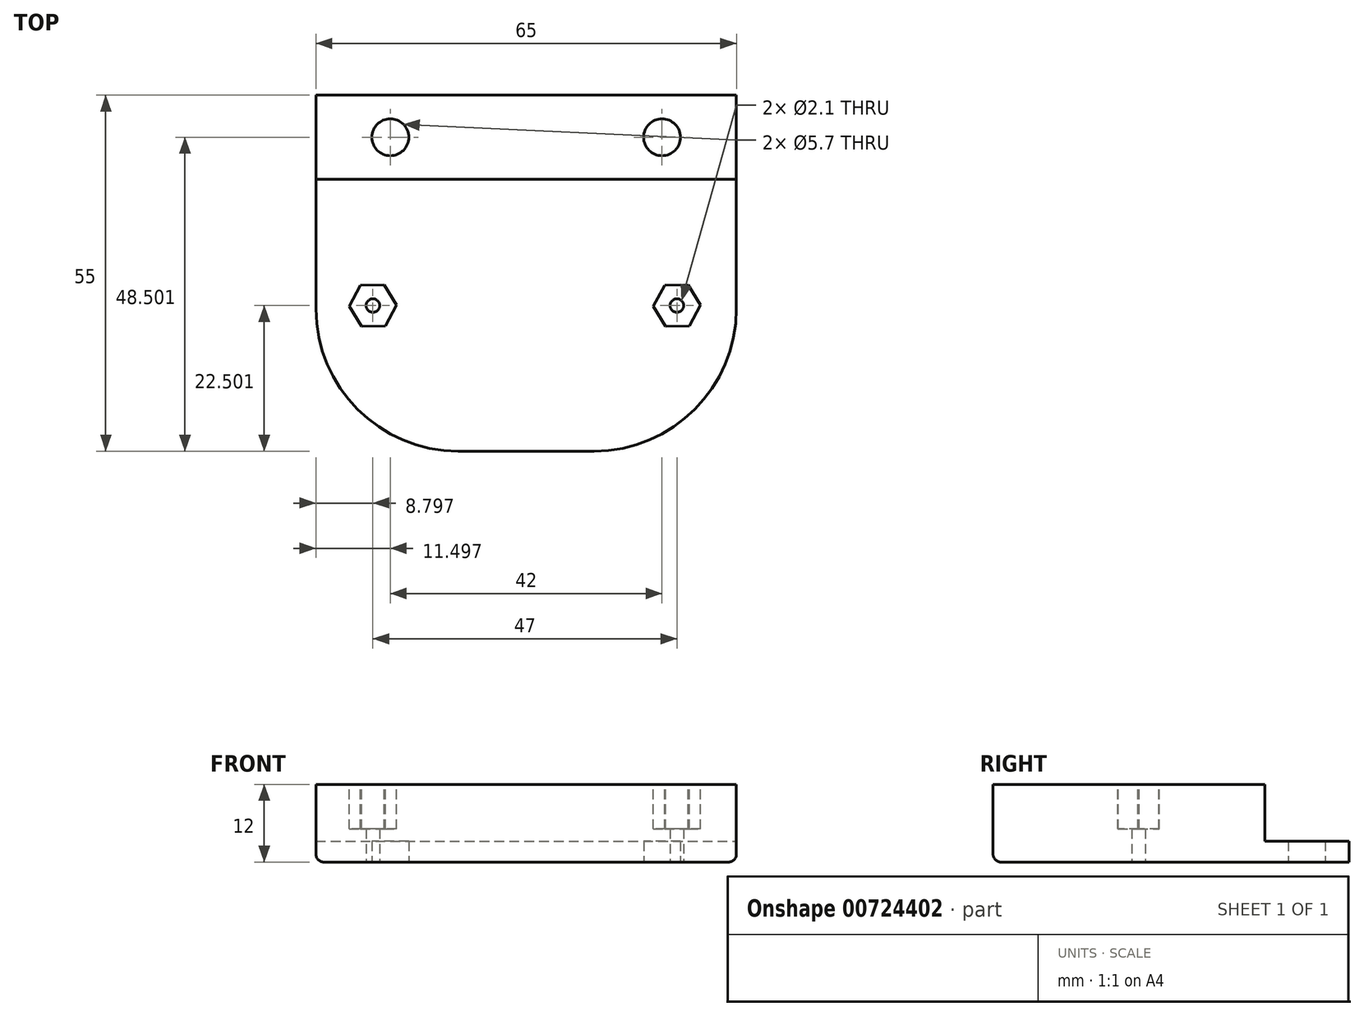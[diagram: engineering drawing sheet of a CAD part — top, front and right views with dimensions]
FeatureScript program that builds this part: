
annotation { "Feature Type Name" : "Feature", "Feature Type Description" : "" }
export const myFeature = defineFeature(function(context is Context, id is Id, definition is map)
    precondition{}
    {
        {
            var Q0;
            Q0=qCreatedBy(makeId("Top.planeOp"),FACE);
            var sketch = newSketch(context, id + "F0", { "sketchPlane" : qUnion([Q0])});
            skLineSegment(sketch, "E0.bottom", {"start": v(-32.1, -2.87) * mm, "end": v(32.9, -2.87) * mm});
            skLineSegment(sketch, "E0.top", {"start": v(-32.1, -17.87) * mm, "end": v(32.9, -17.87) * mm});
            skLineSegment(sketch, "E0.left", {"start": v(-32.1, -2.87) * mm, "end": v(-32.1, -17.87) * mm});
            skLineSegment(sketch, "E0.right", {"start": v(32.9, -2.87) * mm, "end": v(32.9, -17.87) * mm});
            skCircle(sketch, "E1", {"center": v(21.4, -9.37) * mm, "radius": 2.85 * mm});
            skCircle(sketch, "E2", {"center": v(-20.6, -9.37) * mm, "radius": 2.85 * mm});
            skLineSegment(sketch, "E3.top", {"start": v(-10.1, -57.87) * mm, "end": v(10.9, -57.87) * mm});
            skLineSegment(sketch, "E3.left", {"start": v(-32.1, -17.87) * mm, "end": v(-32.1, -35.87) * mm});
            skLineSegment(sketch, "E3.right", {"start": v(32.9, -17.87) * mm, "end": v(32.9, -35.87) * mm});
            skPoint(sketch, "E4.visualSharp", {"position": v(32.9, -57.87) * mm});
            skArc(sketch, "E4.filletArc", {"start": v(10.9, -57.87) * mm, "mid": v(26.45, -51.43) * mm, "end": v(32.9, -35.87) * mm});
            skPoint(sketch, "E5.visualSharp", {"position": v(-32.1, -57.87) * mm});
            skArc(sketch, "E5.filletArc", {"start": v(-32.1, -35.87) * mm, "mid": v(-25.66, -51.43) * mm, "end": v(-10.1, -57.87) * mm});
            skSolve(sketch);
        }
        {
            var Q0;
            Q0 = qSketchRegion(id + "F0", true);
            extrude(context, id + "F1", {"entities" : qUnion([Q0]), "depth" : 12 * mm, "offsetDistance" : 25 * mm});
        }
        {
            var Q0;
            Q0=makeQuery(id+"F1.opExtrude","CAP_FACE",FACE,{"disambiguationData":[OSD([sQuery(id+"F0.wireOp",EDGE,"E0.bottom"),sQuery(id+"F0.wireOp",EDGE,"E0.left"),sQuery(id+"F0.wireOp",EDGE,"E0.right"),sQuery(id+"F0.wireOp",EDGE,"Pb8QJhGn-lq3P-DoKP-Ju5z-BRii3pjlZWMS")])],"isStart":false});
            var sketch = newSketch(context, id + "F2", { "sketchPlane" : qUnion([Q0])});
            skLineSegment(sketch, "E6.bottom", {"start": v(32.9, -15.87) * mm, "end": v(-32.1, -15.87) * mm});
            skLineSegment(sketch, "E6.top", {"start": v(32.9, -2.87) * mm, "end": v(-32.1, -2.87) * mm});
            skLineSegment(sketch, "E6.left", {"start": v(32.9, -15.87) * mm, "end": v(32.9, -2.87) * mm});
            skLineSegment(sketch, "E6.right", {"start": v(-32.1, -15.87) * mm, "end": v(-32.1, -2.87) * mm});
            skSolve(sketch);
        }
        {
            var Q0;
            Q0 = qSketchRegion(id + "F2", true);
            extrude(context, id + "F3", {"entities" : qUnion([Q0]), "operationType" : NewBodyOperationType.REMOVE, "oppositeDirection" : true, "depth" : 8.8 * mm, "offsetDistance" : 25 * mm});
        }
        {
            var Q0;
            Q0=makeQuery(id+"F1.opExtrude","CAP_EDGE",EDGE,{"disambiguationData":[OSD([sQuery(id+"F0.wireOp",EDGE,"E0.left"),sQuery(id+"F0.wireOp",EDGE,"E3.left")])],"isStart":true});
            var Q1;
            Q1=makeQuery(id+"F1.opExtrude","CAP_EDGE",EDGE,{"disambiguationData":[OSD([sQuery(id+"F0.wireOp",EDGE,"E3.top")])],"isStart":true});
            var Q2;
            Q2=makeQuery(id+"F1.opExtrude","CAP_EDGE",EDGE,{"disambiguationData":[OSD([sQuery(id+"F0.wireOp",EDGE,"E0.right"),sQuery(id+"F0.wireOp",EDGE,"E3.right")])],"isStart":true});
            fillet(context, id + "F4", {"entities" : qUnion([Q0, Q1, Q2]), "radius" : 1.2 * mm, "tangentPropagation" : true, "allowEdgeOverflow" : false});
        }
        {
            var Q0;
            Q0=makeQuery(id+"F1.opExtrude","CAP_FACE",FACE,{"disambiguationData":[OSD([sQuery(id+"F0.wireOp",EDGE,"E0.bottom"),sQuery(id+"F0.wireOp",EDGE,"E0.left"),sQuery(id+"F0.wireOp",EDGE,"E0.right"),sQuery(id+"F0.wireOp",EDGE,"E1"),sQuery(id+"F0.wireOp",EDGE,"E2"),sQuery(id+"F0.wireOp",EDGE,"E3.top"),sQuery(id+"F0.wireOp",EDGE,"E3.left"),sQuery(id+"F0.wireOp",EDGE,"E3.right"),sQuery(id+"F0.wireOp",EDGE,"E4.filletArc"),sQuery(id+"F0.wireOp",EDGE,"E5.filletArc")])],"isStart":true});
            var sketch = newSketch(context, id + "F5", { "sketchPlane" : qUnion([Q0])});
            skCircle(sketch, "E7", {"center": v(23.7, 35.37) * mm, "radius": 1.05 * mm});
            skCircle(sketch, "E8", {"center": v(-23.3, 35.37) * mm, "radius": 1.05 * mm});
            skSolve(sketch);
        }
        {
            var Q0;
            Q0 = qSketchRegion(id + "F5", true);
            extrude(context, id + "F6", {"entities" : qUnion([Q0]), "operationType" : NewBodyOperationType.REMOVE, "oppositeDirection" : true, "depth" : 15 * mm, "offsetDistance" : 25 * mm});
        }
        {
            var Q0;
            Q0=makeQuery(id+"F1.opExtrude","CAP_FACE",FACE,{"disambiguationData":[OSD([sQuery(id+"F0.wireOp",EDGE,"E0.bottom"),sQuery(id+"F0.wireOp",EDGE,"E0.left"),sQuery(id+"F0.wireOp",EDGE,"E0.right"),sQuery(id+"F0.wireOp",EDGE,"E1"),sQuery(id+"F0.wireOp",EDGE,"E2"),sQuery(id+"F0.wireOp",EDGE,"E3.top"),sQuery(id+"F0.wireOp",EDGE,"E3.left"),sQuery(id+"F0.wireOp",EDGE,"E3.right"),sQuery(id+"F0.wireOp",EDGE,"E4.filletArc"),sQuery(id+"F0.wireOp",EDGE,"E5.filletArc")])],"isStart":false});
            var sketch = newSketch(context, id + "F7", { "sketchPlane" : qUnion([Q0])});
            skCircle(sketch, "E9.cCircle", {"center": v(23.7, -35.37) * mm, "radius": 3.18 * mm, "construction": true});
            skLineSegment(sketch, "E9.0", {"start": v(27.36, -35.28) * mm, "end": v(25.6, -38.5) * mm});
            skLineSegment(sketch, "E9.1", {"start": v(25.6, -38.5) * mm, "end": v(21.94, -38.59) * mm});
            skLineSegment(sketch, "E9.2", {"start": v(21.94, -38.59) * mm, "end": v(20.03, -35.46) * mm});
            skLineSegment(sketch, "E9.3", {"start": v(20.03, -35.46) * mm, "end": v(21.79, -32.24) * mm});
            skLineSegment(sketch, "E9.4", {"start": v(21.79, -32.24) * mm, "end": v(25.45, -32.15) * mm});
            skLineSegment(sketch, "E9.5", {"start": v(25.45, -32.15) * mm, "end": v(27.36, -35.28) * mm});
            skPoint(sketch, "E9.0.midPoint", {"position": v(26.48, -36.9) * mm});
            skCircle(sketch, "E10.cCircle", {"center": v(-23.3, -35.37) * mm, "radius": 3.18 * mm, "construction": true});
            skLineSegment(sketch, "E10.0", {"start": v(-19.64, -35.28) * mm, "end": v(-21.4, -38.5) * mm});
            skLineSegment(sketch, "E10.1", {"start": v(-21.4, -38.5) * mm, "end": v(-25.06, -38.59) * mm});
            skLineSegment(sketch, "E10.2", {"start": v(-25.06, -38.59) * mm, "end": v(-26.97, -35.46) * mm});
            skLineSegment(sketch, "E10.3", {"start": v(-26.97, -35.46) * mm, "end": v(-25.21, -32.24) * mm});
            skLineSegment(sketch, "E10.4", {"start": v(-25.21, -32.24) * mm, "end": v(-21.55, -32.15) * mm});
            skLineSegment(sketch, "E10.5", {"start": v(-21.55, -32.15) * mm, "end": v(-19.64, -35.28) * mm});
            skPoint(sketch, "E10.0.midPoint", {"position": v(-20.52, -36.9) * mm});
            skSolve(sketch);
        }
        {
            var Q0;
            Q0 = qSketchRegion(id + "F7", true);
            extrude(context, id + "F8", {"entities" : qUnion([Q0]), "operationType" : NewBodyOperationType.REMOVE, "oppositeDirection" : true, "depth" : 6.9 * mm, "offsetDistance" : 25 * mm});
        }
    });
